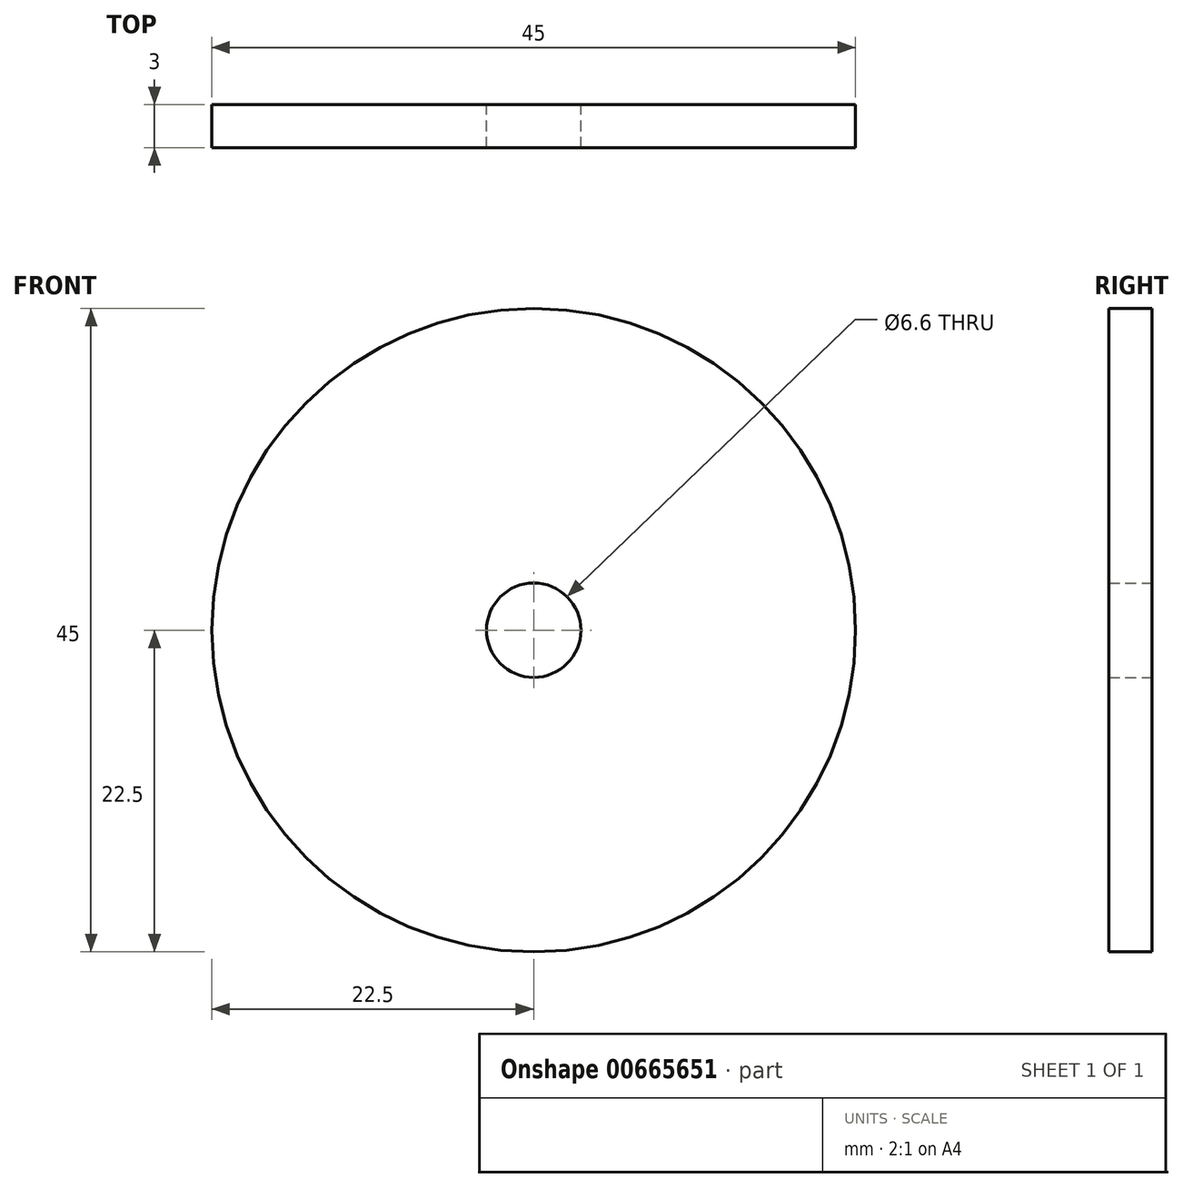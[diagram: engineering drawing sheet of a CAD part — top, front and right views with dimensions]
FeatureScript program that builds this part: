
annotation { "Feature Type Name" : "Feature", "Feature Type Description" : "" }
export const myFeature = defineFeature(function(context is Context, id is Id, definition is map)
    precondition{}
    {
        {
            var Q0;
            Q0=qCreatedBy(makeId("Front.planeOp"),FACE);
            var sketch = newSketch(context, id + "F0", { "sketchPlane" : qUnion([Q0])});
            skCircle(sketch, "E0", {"center": v(0, 0) * mm, "radius": 22.5 * mm});
            skCircle(sketch, "E1", {"center": v(0, 0) * mm, "radius": 3.3 * mm});
            skSolve(sketch);
        }
        {
            var Q0;
            Q0 = qSketchRegion(id + "F0", true);
            extrude(context, id + "F1", {"entities" : qUnion([Q0]), "depth" : 3 * mm, "offsetDistance" : 25 * mm});
        }
    });
